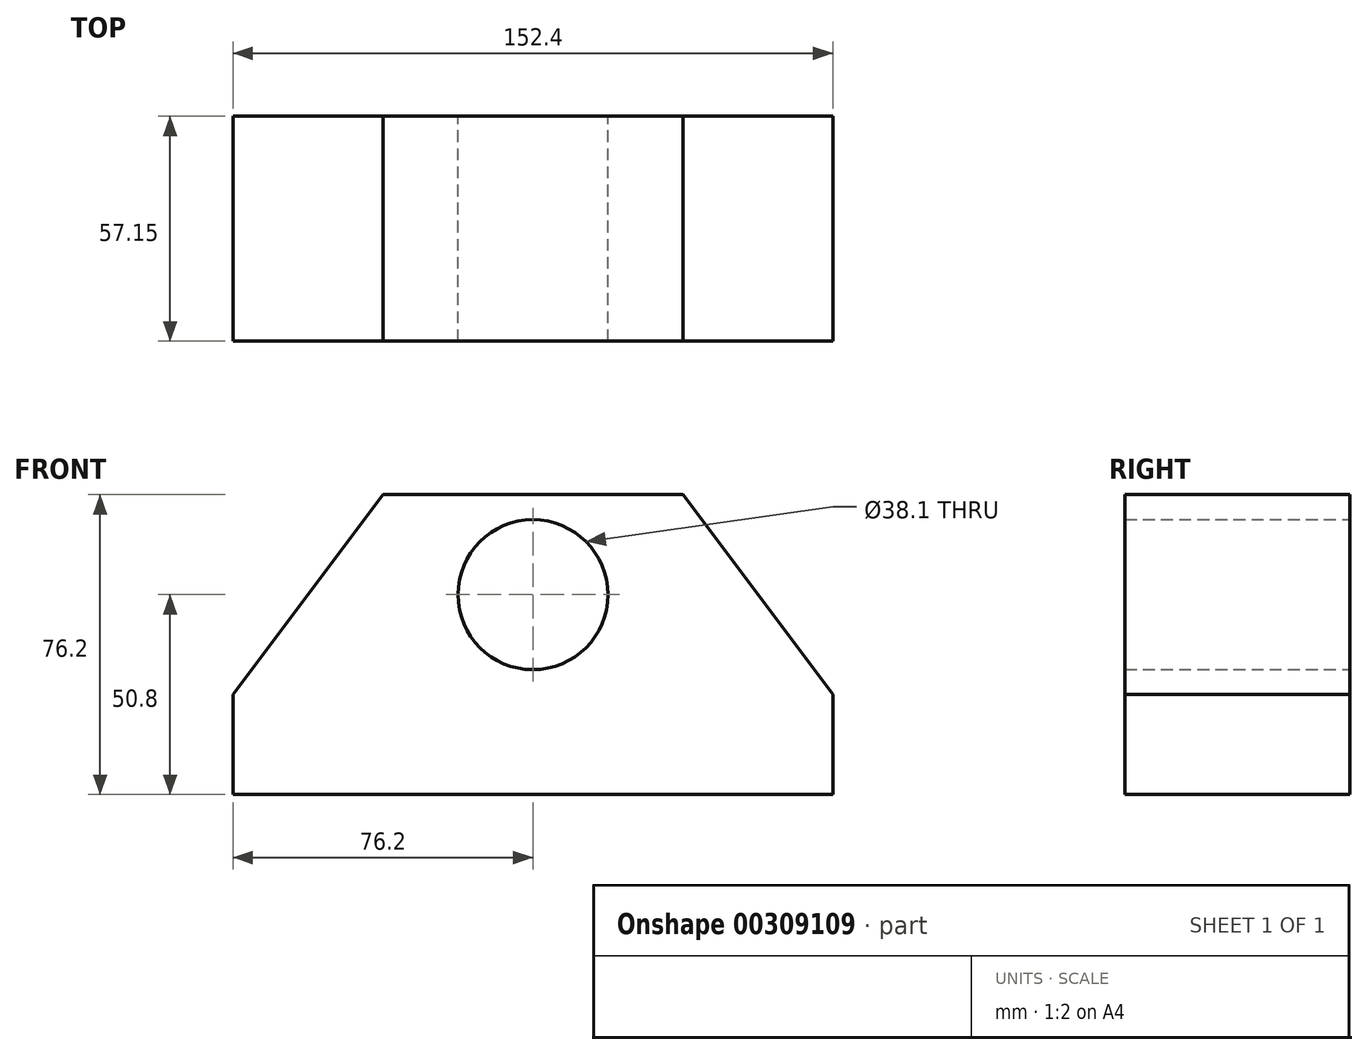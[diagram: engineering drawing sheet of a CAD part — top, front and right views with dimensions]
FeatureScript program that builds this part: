
annotation { "Feature Type Name" : "Feature", "Feature Type Description" : "" }
export const myFeature = defineFeature(function(context is Context, id is Id, definition is map)
    precondition{}
    {
        {
            var Q0;
            Q0=qCreatedBy(makeId("Front.planeOp"),FACE);
            var sketch = newSketch(context, id + "F0", { "sketchPlane" : qUnion([Q0])});
            skCircle(sketch, "E0", {"center": v(0, 0) * mm, "radius": 19.05 * mm});
            skLineSegment(sketch, "E1.top", {"start": v(-76.2, -50.8) * mm, "end": v(76.2, -50.8) * mm});
            skLineSegment(sketch, "E1.left", {"start": v(-76.2, -25.4) * mm, "end": v(-76.2, -50.8) * mm});
            skLineSegment(sketch, "E1.right", {"start": v(76.2, -25.4) * mm, "end": v(76.2, -50.8) * mm});
            skLineSegment(sketch, "E2", {"start": v(0, 25.4) * mm, "end": v(-38.1, 25.4) * mm});
            skLineSegment(sketch, "E3", {"start": v(0, 25.4) * mm, "end": v(38.1, 25.4) * mm});
            skLineSegment(sketch, "E4", {"start": v(-38.1, 25.4) * mm, "end": v(-76.2, -25.4) * mm});
            skLineSegment(sketch, "E5", {"start": v(38.1, 25.4) * mm, "end": v(76.2, -25.4) * mm});
            skPoint(sketch, "E1.bottom.start.orphan", {"position": v(0, -19.05) * mm});
            skSolve(sketch);
        }
        {
            var Q0;
            Q0 = qSketchRegion(id + "F0", true);
            extrude(context, id + "F1", {"entities" : qUnion([Q0]), "depth" : 57.15 * mm});
        }
    });
